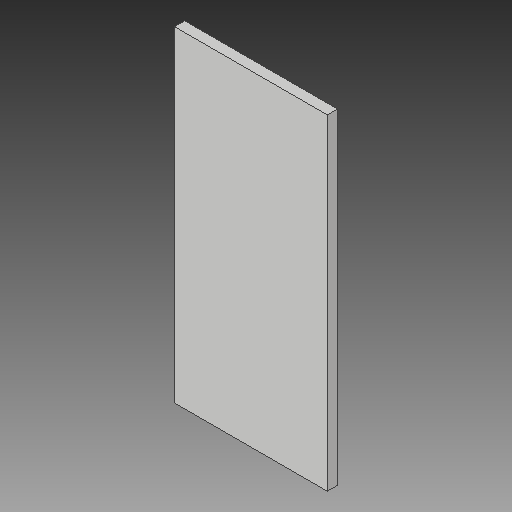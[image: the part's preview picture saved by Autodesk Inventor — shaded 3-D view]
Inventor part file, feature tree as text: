
AUTODESK INVENTOR PART (.ipt)
format: ipt  version: 2017 (Build 210142000, 142)  size: 91,136 bytes
history: native  units: mm
features: other x1, extrude x1, sketch x1
ambient origin geometry x8: Origin, YZ Plane, XZ Plane, XY Plane, X Axis, Y Axis, Z Axis, Center Point
bodies: Body1 (feature_tree)
feature tree (3):
  other  "Sólido1"
  extrude  "Extrusión1"  Depth=75.0mm
  sketch  "Boceto1"  dims[d0=160.0mm d1=75.0mm d2=5.0mm d3=0.0mm]
